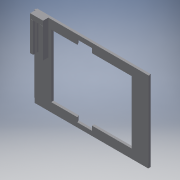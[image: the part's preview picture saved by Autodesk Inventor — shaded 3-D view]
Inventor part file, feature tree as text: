
AUTODESK INVENTOR PART (.ipt)
format: ipt  version: 2018.3 (Build 223284000, 284)  size: 240,640 bytes
history: native  units: mm
features: extrude x12, sketch x12, chamfer x2
ambient origin geometry x8: Origin, YZ Plane, XZ Plane, XY Plane, X Axis, Y Axis, Z Axis, Center Point
bodies: Solid1 (feature_tree)
feature tree (26):
  extrude  "Extrusion1"  Depth=2.8mm
  extrude  "Extrusion2"  Depth=0.7mm
  extrude  "Extrusion3"  Depth=0.7mm
  extrude  "Extrusion4"  Depth=85.0mm TaperAngle=0.0deg
  extrude  "Extrusion5"  Depth=5.42mm
  extrude  "Extrusion6"  Depth=0.6mm TaperAngle=0.0deg
  extrude  "Extrusion7"  Depth=1.25mm
  extrude  "Extrusion8"  Depth=33.0mm
  extrude  "Extrusion9"  Depth=2.0mm
  extrude  "Extrusion10"  Depth=6.0mm TaperAngle=0.0deg
  extrude  "Extrusion11"  Depth=2.0mm
  extrude  "Extrusion13"  Depth=33.0mm TaperAngle=0.0deg
  chamfer  "Chamfer1"  Distance=1.65mm
  chamfer  "Chamfer2"  Distance=1.6mm
  sketch  "Sketch1"  dims[d0=126.5mm d1=2.8mm]
  sketch  "Sketch2"  dims[d2=90.0mm d3=0.0mm d4=0.7mm]
  sketch  "Sketch3"  dims[d5=1.4mm d6=0.7mm]
  sketch  "Sketch4"  dims[d7=1.4mm d8=85.0mm d9=0.0mm]
  sketch  "Sketch5"  dims[d12=14.5mm d13=5.42mm]
  sketch  "Sketch6"  dims[d14=0.6mm d15=5.72mm d16=0.0mm]
  sketch  "Sketch7"  dims[d17=1.25mm d18=1.25mm]
  sketch  "Sketch8"  dims[d19=0.15mm d20=0.0mm d21=33.0mm]
  sketch  "Sketch9"  dims[d22=2.0mm d23=2.0mm]
  sketch  "Sketch10"  dims[d24=10.5mm d25=6.0mm d26=0.0mm]
  sketch  "Sketch11"  dims[d27=4.0mm d28=2.0mm]
  sketch  "Sketch12"  dims[d29=1.5mm d30=33.0mm d31=0.0mm d32=1.65mm d33=1.6mm d34=33.0mm d35=0.0mm d36=1.5mm d37=2.0mm d38=33.0mm d39=0.0mm d40=1.65mm d41=1.6mm d42=33.0mm d43=0.0mm d47=1.5mm d48=0.0mm d49=1.5mm d50=0.0mm d51=90.0mm d52=70.0mm d55=18.25mm d56=18.25mm d57=10.0mm d58=10.0mm d59=16.43mm d60=5.0mm d61=29.07mm d62=1.5mm d63=0.0mm d64=1.2mm d65=2.0mm d66=60.0deg d67=5.0mm d68=29.07mm d69=1.2mm d70=2.0mm d71=60.0deg]
